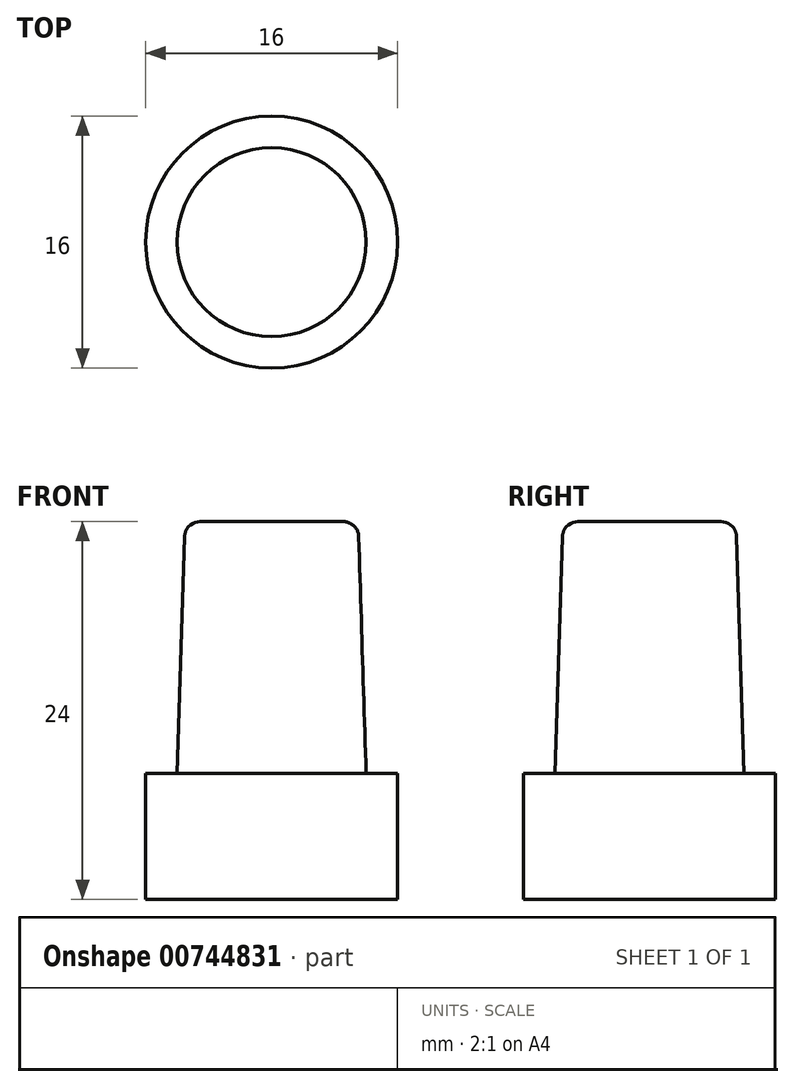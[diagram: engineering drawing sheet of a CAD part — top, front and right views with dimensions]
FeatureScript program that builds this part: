
annotation { "Feature Type Name" : "Feature", "Feature Type Description" : "" }
export const myFeature = defineFeature(function(context is Context, id is Id, definition is map)
    precondition{}
    {
        {
            var Q0;
            Q0=qCreatedBy(makeId("Top.planeOp"),FACE);
            var sketch = newSketch(context, id + "F0", { "sketchPlane" : qUnion([Q0])});
            skCircle(sketch, "E0", {"center": v(0, 0) * mm, "radius": 8 * mm});
            skSolve(sketch);
        }
        {
            var Q0;
            Q0=makeQuery(id+"F0.imprint","IMPRINT",FACE,{"disambiguationData":[TD([[makeQuery(id+"F0.imprint","IMPRINT",EDGE,{"derivedFrom":sQuery(id+"F0.wireOp",EDGE,"E0")}),1.0]])]});
            extrude(context, id + "F1", {"entities" : qUnion([Q0]), "depth" : 8 * mm, "offsetDistance" : 25 * mm});
        }
        {
            var Q0;
            Q0=makeQuery(id+"F1.opExtrude","CAP_FACE",FACE,{"disambiguationData":[OSD([sQuery(id+"F0.wireOp",EDGE,"E0")])],"isStart":false});
            var sketch = newSketch(context, id + "F2", { "sketchPlane" : qUnion([Q0])});
            skCircle(sketch, "E1", {"center": v(0, 0) * mm, "radius": 6 * mm});
            skSolve(sketch);
        }
        {
            var Q0;
            Q0=makeQuery(id+"F2.imprint","IMPRINT",FACE,{"disambiguationData":[TD([[makeQuery(id+"F2.imprint","IMPRINT",EDGE,{"derivedFrom":sQuery(id+"F2.wireOp",EDGE,"E1")}),-1.0]])]});
            cPlane(context, id + "F3", {"entities" : qUnion([Q0]), "cplaneType" : CPlaneType.OFFSET, "offset" : 16 * mm, "width" : 150 * mm, "height" : 150 * mm});
        }
        {
            var Q0;
            Q0=qCreatedBy(id+"F3.planeOp",FACE);
            var sketch = newSketch(context, id + "F4", { "sketchPlane" : qUnion([Q0])});
            skCircle(sketch, "E2", {"center": v(0, 0) * mm, "radius": 5.5 * mm});
            skSolve(sketch);
        }
        {
            var Q1;
            Q1=makeQuery(id+"F2.imprint","IMPRINT",FACE,{"disambiguationData":[TD([[makeQuery(id+"F2.imprint","IMPRINT",EDGE,{"derivedFrom":sQuery(id+"F2.wireOp",EDGE,"E1")}),1.0]])]});
            var Q2;
            Q2=makeQuery(id+"F4.imprint","IMPRINT",FACE,{"disambiguationData":[TD([[makeQuery(id+"F4.imprint","IMPRINT",EDGE,{"derivedFrom":sQuery(id+"F4.wireOp",EDGE,"E2")}),1.0]])]});
            loft(context, id + "F5", {"operationType" : NewBodyOperationType.ADD, "sheetProfilesArray" : [{ "sheetProfileEntities" : qUnion([Q1]) }, { "sheetProfileEntities" : qUnion([Q2]) }]});
        }
        {
            var Q0;
            Q0=makeQuery(id+"F5.opLoft","MID_CAP_EDGE",EDGE,{"disambiguationData":[OSD([sQuery(id+"F4.wireOp",EDGE,"E2")])],"capPos":1.0});
            fillet(context, id + "F6", {"entities" : qUnion([Q0]), "radius" : 1 * mm, "tangentPropagation" : true, "allowEdgeOverflow" : false});
        }
    });
